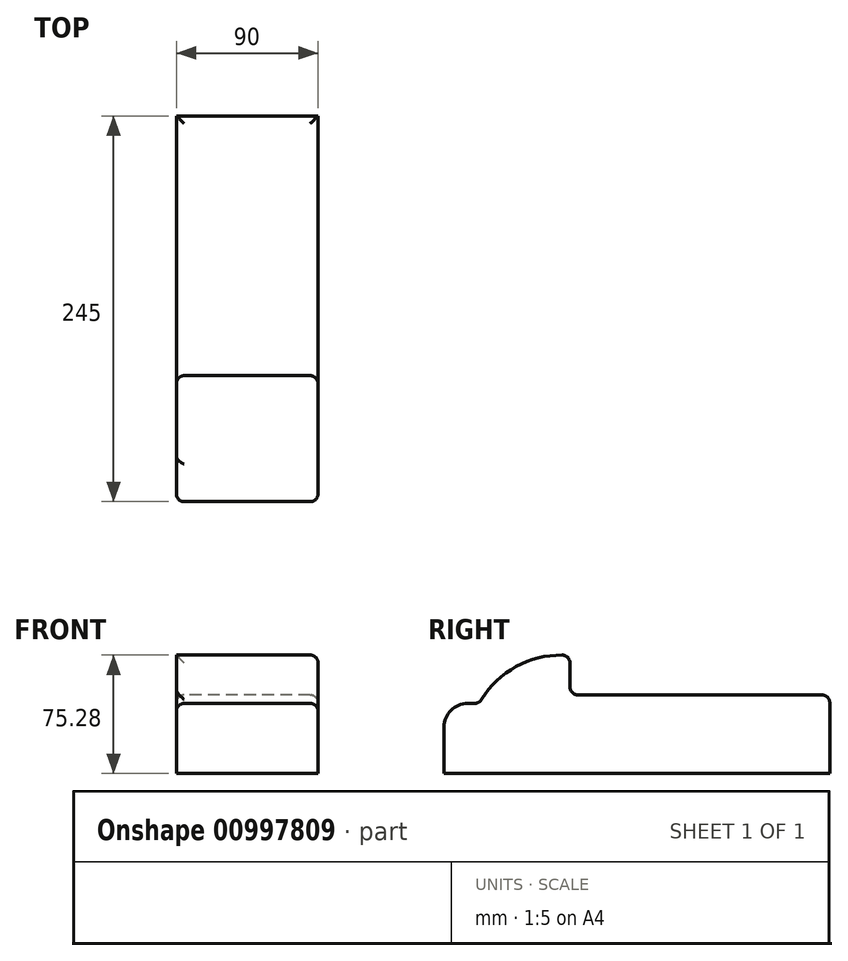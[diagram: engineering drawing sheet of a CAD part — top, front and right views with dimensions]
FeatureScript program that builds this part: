
annotation { "Feature Type Name" : "Feature", "Feature Type Description" : "" }
export const myFeature = defineFeature(function(context is Context, id is Id, definition is map)
    precondition{}
    {
        {
            var Q0;
            Q0=qCreatedBy(makeId("Right.planeOp"),FACE);
            var sketch = newSketch(context, id + "F0", { "sketchPlane" : qUnion([Q0])});
            skLineSegment(sketch, "E0", {"start": v(0, 0) * mm, "end": v(245, 0) * mm});
            skLineSegment(sketch, "E1", {"start": v(245, 0) * mm, "end": v(245, 50) * mm});
            skLineSegment(sketch, "E2", {"start": v(245, 50) * mm, "end": v(80, 50) * mm});
            skLineSegment(sketch, "E3", {"start": v(80, 50) * mm, "end": v(80, 75) * mm});
            skLineSegment(sketch, "E4", {"start": v(80, 75) * mm, "end": v(80, 75) * mm});
            skLineSegment(sketch, "E5", {"start": v(0, 15) * mm, "end": v(0, 0) * mm});
            skArc(sketch, "E6", {"start": v(80, 75) * mm, "mid": v(46.63, 68.46) * mm, "end": v(22.36, 44.63) * mm});
            skArc(sketch, "E7", {"start": v(97.13, 136.6) * mm, "mid": v(95.43, 140.1) * mm, "end": v(95.45, 136.2) * mm});
            skLineSegment(sketch, "E8", {"start": v(22.36, 44.63) * mm, "end": v(0, 44.63) * mm});
            skLineSegment(sketch, "E9", {"start": v(0, 44.63) * mm, "end": v(0, 0) * mm});
            skSolve(sketch);
        }
        {
            var Q0;
            {var subQ0=sQuery(id+"F0.wireOp",EDGE,"E0");Q0=makeQuery(id+"F0.imprint","IMPRINT",FACE,{"disambiguationData":[TD([[makeQuery(id+"F0.imprint","IMPRINT",EDGE,{"derivedFrom":subQ0}),1.0]])]});}
            extrude(context, id + "F1", {"entities" : qUnion([Q0]), "depth" : 90 * mm, "offsetDistance" : 25 * mm});
        }
        {
            var Q0;
            Q0=makeQuery(id+"F1.opExtrude","SWEPT_EDGE",EDGE,{"disambiguationData":[OSD([sQuery(id+"F0.wireOp",EDGE,"E8"),sQuery(id+"F0.wireOp",EDGE,"E9")])]});
            fillet(context, id + "F2", {"entities" : qUnion([Q0]), "radius" : 15 * mm, "tangentPropagation" : true, "allowEdgeOverflow" : false});
        }
        {
            var Q0;
            Q0=makeQuery(id+"F1.opExtrude","CAP_EDGE",EDGE,{"disambiguationData":[OSD([sQuery(id+"F0.wireOp",EDGE,"E6")])],"isStart":false});
            var Q1;
            Q1=makeQuery(id+"F1.opExtrude","CAP_EDGE",EDGE,{"disambiguationData":[OSD([sQuery(id+"F0.wireOp",EDGE,"E2")])],"isStart":false});
            var Q2;
            Q2=makeQuery(id+"F1.opExtrude","CAP_EDGE",EDGE,{"disambiguationData":[OSD([sQuery(id+"F0.wireOp",EDGE,"E8")])],"isStart":false});
            var Q3;
            Q3=makeQuery(id+"F1.opExtrude","SWEPT_EDGE",EDGE,{"disambiguationData":[OSD([sQuery(id+"F0.wireOp",EDGE,"E6"),sQuery(id+"F0.wireOp",EDGE,"E8")])]});
            var Q4;
            Q4=makeQuery(id+"F1.opExtrude","CAP_EDGE",EDGE,{"disambiguationData":[OSD([sQuery(id+"F0.wireOp",EDGE,"E8")])],"isStart":true});
            var Q5;
            Q5=makeQuery(id+"F1.opExtrude","CAP_EDGE",EDGE,{"disambiguationData":[OSD([sQuery(id+"F0.wireOp",EDGE,"E3")])],"isStart":true});
            var Q6;
            Q6=makeQuery(id+"F1.opExtrude","CAP_EDGE",EDGE,{"disambiguationData":[OSD([sQuery(id+"F0.wireOp",EDGE,"E2")])],"isStart":true});
            var Q7;
            Q7=makeQuery(id+"F1.opExtrude","SWEPT_EDGE",EDGE,{"disambiguationData":[OSD([sQuery(id+"F0.wireOp",EDGE,"E1"),sQuery(id+"F0.wireOp",EDGE,"E2")])]});
            var Q8;
            Q8=makeQuery(id+"F1.opExtrude","CAP_EDGE",EDGE,{"disambiguationData":[OSD([sQuery(id+"F0.wireOp",EDGE,"E3")])],"isStart":false});
            var Q9;
            Q9=makeQuery(id+"F1.opExtrude","SWEPT_EDGE",EDGE,{"disambiguationData":[OSD([sQuery(id+"F0.wireOp",EDGE,"E3"),sQuery(id+"F0.wireOp",EDGE,"E6")])]});
            var Q10;
            Q10=makeQuery(id+"F1.opExtrude","SWEPT_EDGE",EDGE,{"disambiguationData":[OSD([sQuery(id+"F0.wireOp",EDGE,"E2"),sQuery(id+"F0.wireOp",EDGE,"E3")])]});
            fillet(context, id + "F3", {"entities" : qUnion([Q0, Q1, Q2, Q3, Q4, Q5, Q6, Q7, Q8, Q9, Q10]), "radius" : 5 * mm, "tangentPropagation" : true, "allowEdgeOverflow" : false});
        }
    });
